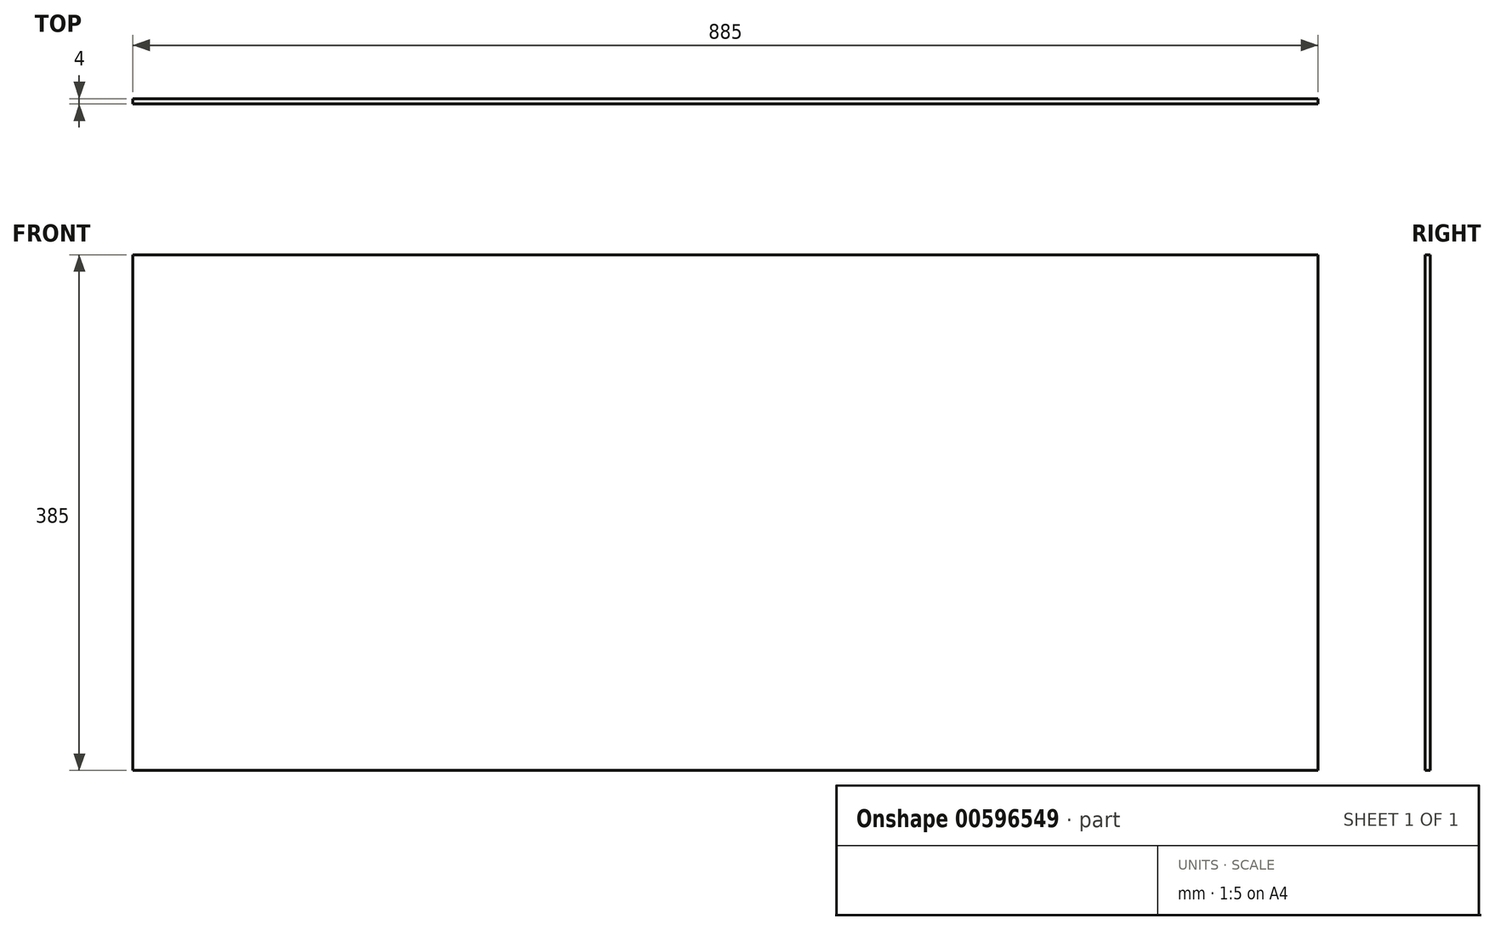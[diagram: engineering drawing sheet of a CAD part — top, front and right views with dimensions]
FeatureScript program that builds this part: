
annotation { "Feature Type Name" : "Feature", "Feature Type Description" : "" }
export const myFeature = defineFeature(function(context is Context, id is Id, definition is map)
    precondition{}
    {
        {
            var Q0;
            Q0=qCreatedBy(makeId("Front.planeOp"),FACE);
            var sketch = newSketch(context, id + "F0", { "sketchPlane" : qUnion([Q0])});
            skLineSegment(sketch, "E0.bottom", {"start": v(0, 0) * mm, "end": v(885, 0) * mm});
            skLineSegment(sketch, "E0.top", {"start": v(0, 385) * mm, "end": v(885, 385) * mm});
            skLineSegment(sketch, "E0.left", {"start": v(0, 0) * mm, "end": v(0, 385) * mm});
            skLineSegment(sketch, "E0.right", {"start": v(885, 0) * mm, "end": v(885, 385) * mm});
            skSolve(sketch);
        }
        {
            var Q0;
            Q0=qSketchRegion(id+"F0",true);
            extrude(context, id + "F1", {"entities" : qUnion([Q0]), "depth" : 4 * mm, "offsetDistance" : 25 * mm});
        }
    });
